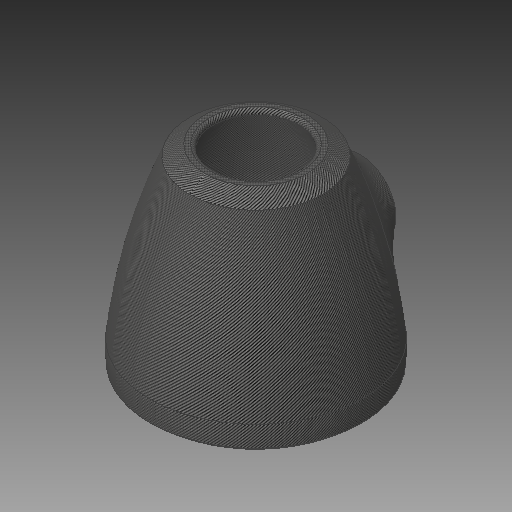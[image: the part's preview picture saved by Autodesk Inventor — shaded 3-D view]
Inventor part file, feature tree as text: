
AUTODESK INVENTOR PART (.ipt)
format: ipt  version: 2018 (Build 220112000, 112)  size: 394,752 bytes
history: native  units: mm
features: sketch x4, extrude x3, fillet x3, chamfer x2, revolve x1
ambient origin geometry x8: Origin, YZ Plane, XZ Plane, XY Plane, X Axis, Y Axis, Z Axis, Center Point
bodies: Solid1 (feature_tree)
feature tree (13):
  revolve  "Revolution1"  [1 undecoded]
  extrude  "Extrusion1"  Depth=135.0mm
  extrude  "Extrusion2"  Depth=145.0mm TaperAngle=0.0deg
  extrude  "Extrusion3"  Depth=5.0mm
  fillet  "Fillet1"  Radius=113.25mm
  fillet  "Fillet2"  Radius=90.0mm
  chamfer  "Chamfer1"  Distance=30.0mm
  fillet  "Fillet3"  Radius=135.0mm
  chamfer  "Chamfer2"  Distance=5.0mm
  sketch  "Sketch1"  dims[d2=30.0mm d3=270.0mm]
  sketch  "Sketch2"  dims[d4=90.0deg d5=135.0mm]
  sketch  "Sketch3"  dims[d6=100.0mm d7=145.0mm d8=0.0mm]
  sketch  "Sketch4"  dims[d9=135.0mm d10=100.0mm d11=113.25mm d12=0.0mm d13=90.0mm d14=30.0mm d15=0.0mm d16=135.0mm d17=5.0mm d18=7.25mm d19=2.0mm d20=45.0deg d21=5.0mm d22=15.5mm d23=2.0mm d24=45.0deg]
note: 1 required parameter value undecoded (feature->parameter linkage not recoverable at this tier; creation-order binding heuristic only, values carry confidence <= 0.55)
